# Revit family: Fixtrue
name_source: partatom
category: Lighting Fixtures
revit_build: Autodesk Revit 2017 (Build: 20160225_1515(x64)
units: mm (PartAtom-declared; Revit-internal decimal feet)

## family parameters
Always vertical = No
Cut with Voids When Loaded = No
Light Source = Yes
OmniClass Number = 23.80.70.00
OmniClass Title = Lighting
Part Type = Normal
Room Calculation Point = No
Round Connector Dimension = Use Diameter
Shared = No
Work Plane-Based = Yes

## types (4) — shared parameters
Color Filter = 16777215
Default Elevation = 1219 mm
Dimming Lamp Color Temperature Shift = <None>
Light Source Symbol Size = 610 mm

## per-type parameters (varying)
| type | Angle of Fixture | Fixture Depth | Fixture Depth / 2 | Fixture Width | Fixture Width / 2 | Inner Elipse Depth | Inner Elipse Width |
| 90 Degree | 90.00° | 800 mm  [stored 2.62467 ft] | 400 mm  [stored 1.31234 ft] | 1920 mm  [stored 6.29921 ft] | 960 mm  [stored 3.14961 ft] | 720 mm | 1840 mm  [stored 6.03675 ft] |
| 110 Degree | 110.00° | 400 mm  [stored 1.31234 ft] | 200 mm  [stored 0.656168 ft] | 1461 mm | 731 mm | 320 mm  [stored 1.04987 ft] | 1381 mm |
| 100 Degree | 100.00° | 400 mm  [stored 1.31234 ft] | 200 mm  [stored 0.656168 ft] | 1461 mm | 731 mm | 320 mm  [stored 1.04987 ft] | 1381 mm |
| 95 Degree | 95.00° | 400 mm  [stored 1.31234 ft] | 200 mm  [stored 0.656168 ft] | 1461 mm | 731 mm | 320 mm  [stored 1.04987 ft] | 1381 mm |

note: [stored X ft] marks values corroborated as IEEE doubles in the binary element streams (Revit-internal decimal feet)

## geometry (parser evidence)
native form markers: Sweep x2
no freeform markers — native parametric forms only
